# Revit family: QF_BOURGEAT_chariot_cafeteria_24plateaux_cote_a_cote_modele_haut_gris
name_source: partatom
category: Equipement spécialisé
revit_build: Autodesk Revit 2015 (Build: 20140606_1530(x64)
units: mm (PartAtom-declared; Revit-internal decimal feet)

## types (3) — shared parameters
Charge max = 120.00 kg
Fabricant = BOURGEAT
Hauteur hors tout = 1700 mm  [stored 5.57743 ft]
Longueur hors tout = 925 mm  [stored 3.03478 ft]
Profondeur hors tout = 620 mm  [stored 2.03412 ft]
Spécification du Fabricant = CHARIOT CAFETERIA
URL catalogue = http://www.bourgeat.fr

## per-type parameters (varying)
| type | Modèle | Poids net à vide | panneaux_fond_gris | panneaux_lateraux_gris |
| chariot_modele_haut_glissieres_grises_sans_panneaux | 783306 | 30.00 kg | Non | Non |
| chariot_modele_haut_glissieres_grises_avec_2_panneaux_gris | 784906 | 36.00 kg | Non | Oui |
| chariot_modele_haut_glissieres_grises_avec_3_panneaux_gris | 784903 | 39.00 kg | Oui | Oui |

note: [stored X ft] marks values corroborated as IEEE doubles in the binary element streams (Revit-internal decimal feet)
